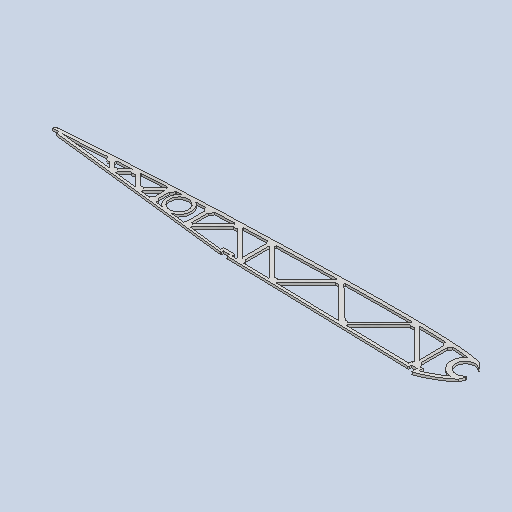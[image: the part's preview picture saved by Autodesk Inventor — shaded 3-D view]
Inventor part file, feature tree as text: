
AUTODESK INVENTOR PART (.ipt)
format: ipt  version: 2022 (Build 260153000, 153)  size: 478,208 bytes
history: native  units: mm
features: extrude x1, sketch x1
ambient origin geometry x8: Origin, YZ Plane, XZ Plane, XY Plane, X Axis, Y Axis, Z Axis, Center Point
bodies: Body1 (feature_tree)
feature tree (2):
  extrude  "Extrusion5"  Depth=10.0mm
  sketch  "Sketch1"  dims[d31=34.456mm d50=368.759386mm d57=16.0mm d69=8.0mm d80=19.0mm d81=16.0mm d82=1.0mm d83=1.0mm d84=1.0mm d85=1.0mm d86=1.0mm d87=0.8mm d88=1.0mm d94=5.0mm d95=5.0mm d105=5.0mm d106=5.0mm d108=2.0mm d114=5.0mm d115=5.0mm d116=24.0mm d117=2.5mm d118=2.5mm d123=2.5mm d124=2.5mm d125=10.0mm d126=24.0mm d127=24.0mm d128=27.0mm d135=0.5mm d139=7.0mm d169=27.0mm d181=45.0deg d185=7.0mm d186=45.0deg d190=7.0mm d191=45.0deg d206=90.0deg d212=90.0deg d215=7.0mm d216=90.0deg d219=7.0mm d220=21.0mm d221=2.0mm d222=0.0mm]
